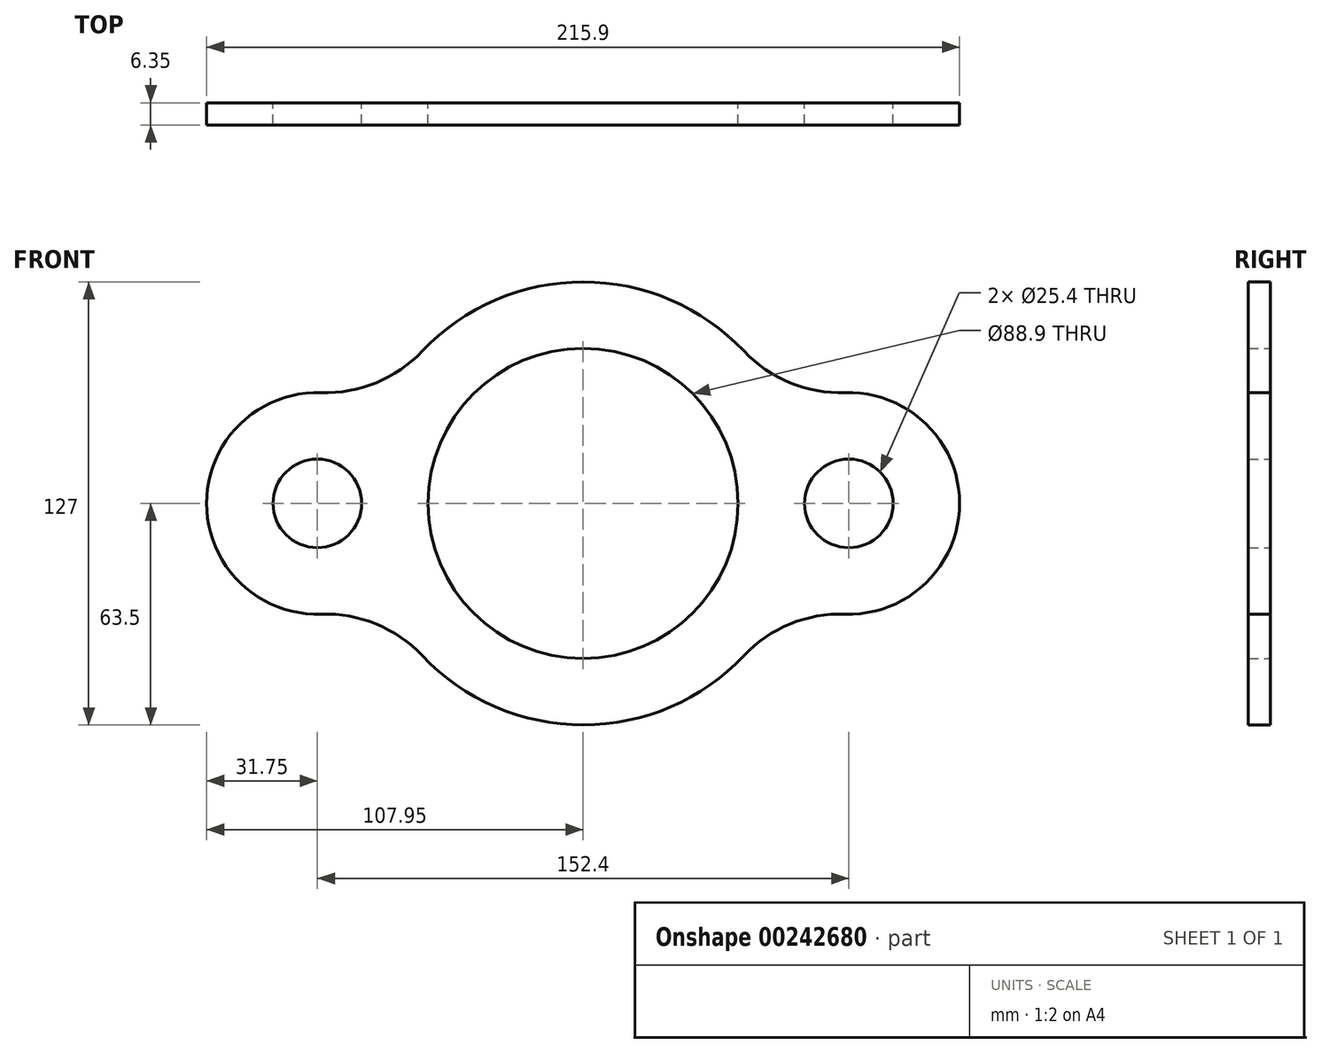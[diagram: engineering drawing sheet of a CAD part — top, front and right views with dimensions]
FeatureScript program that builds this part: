
annotation { "Feature Type Name" : "Feature", "Feature Type Description" : "" }
export const myFeature = defineFeature(function(context is Context, id is Id, definition is map)
    precondition{}
    {
        {
            var Q0;
            Q0=qCreatedBy(makeId("Front.planeOp"),FACE);
            var sketch = newSketch(context, id + "F0", { "sketchPlane" : qUnion([Q0])});
            skArc(sketch, "E0", {"start": v(-46.14, -43.63) * mm, "mid": v(0, -63.5) * mm, "end": v(46.14, -43.63) * mm});
            skArc(sketch, "E1", {"start": v(75.12, -31.73) * mm, "mid": v(107.95, 0) * mm, "end": v(75.12, 31.73) * mm});
            skArc(sketch, "E2", {"start": v(-75.12, 31.73) * mm, "mid": v(-107.95, 0) * mm, "end": v(-75.12, -31.73) * mm});
            skCircle(sketch, "E3", {"center": v(0, 0) * mm, "radius": 44.45 * mm});
            skCircle(sketch, "E4", {"center": v(-76.2, 0) * mm, "radius": 12.7 * mm});
            skCircle(sketch, "E5", {"center": v(76.2, 0) * mm, "radius": 12.7 * mm});
            skPoint(sketch, "E6.visualSharp", {"position": v(-57.94, 25.98) * mm});
            skArc(sketch, "E6.filletArc", {"start": v(-75.12, 31.73) * mm, "mid": v(-59.35, 34.56) * mm, "end": v(-46.14, 43.63) * mm});
            skArc(sketch, "E7.trimOffspring", {"start": v(46.14, 43.63) * mm, "mid": v(0, 63.5) * mm, "end": v(-46.14, 43.63) * mm});
            skPoint(sketch, "E8.visualSharp", {"position": v(-57.94, -25.98) * mm});
            skArc(sketch, "E8.filletArc", {"start": v(-46.14, -43.63) * mm, "mid": v(-59.35, -34.56) * mm, "end": v(-75.12, -31.73) * mm});
            skPoint(sketch, "E9.visualSharp", {"position": v(57.94, 25.98) * mm});
            skArc(sketch, "E9.filletArc", {"start": v(46.14, 43.63) * mm, "mid": v(59.35, 34.56) * mm, "end": v(75.12, 31.73) * mm});
            skPoint(sketch, "E10.visualSharp", {"position": v(57.94, -25.98) * mm});
            skArc(sketch, "E10.filletArc", {"start": v(75.12, -31.73) * mm, "mid": v(59.35, -34.56) * mm, "end": v(46.14, -43.63) * mm});
            skSolve(sketch);
        }
        {
            var Q0;
            Q0=makeQuery(id+"F0.imprint","IMPRINT",FACE,{"disambiguationData":[TD([[makeQuery(id+"F0.imprint","IMPRINT",EDGE,{"derivedFrom":sQuery(id+"F0.wireOp",EDGE,"E0")}),1.0]])]});
            extrude(context, id + "F1", {"entities" : qUnion([Q0]), "depth" : 6.35 * mm});
        }
    });
